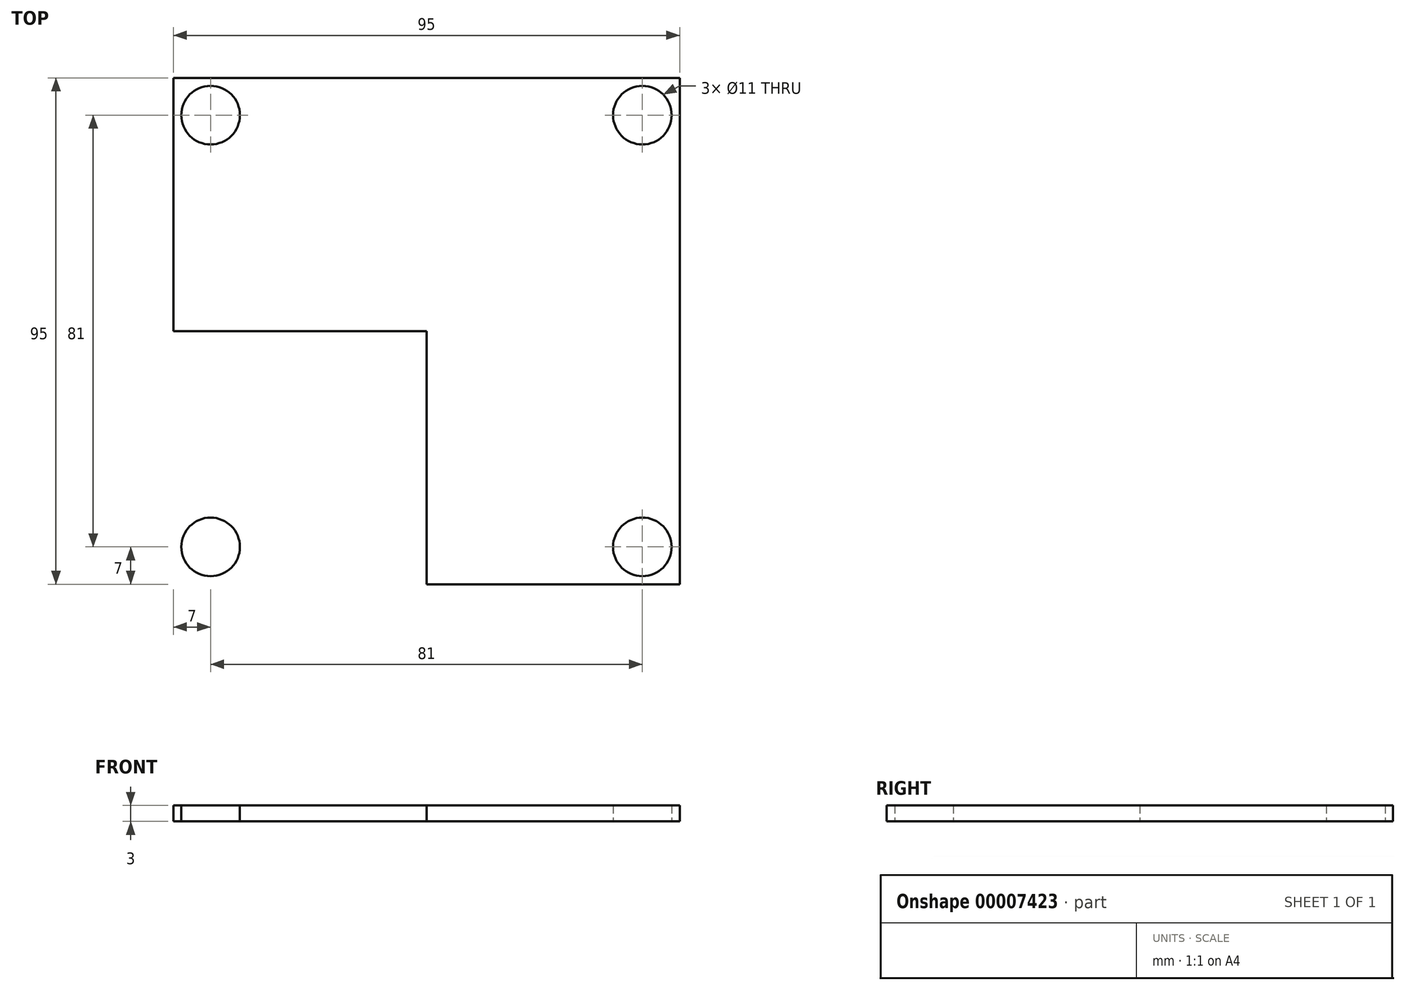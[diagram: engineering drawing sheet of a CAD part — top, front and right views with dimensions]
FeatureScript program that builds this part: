
annotation { "Feature Type Name" : "Feature", "Feature Type Description" : "" }
export const myFeature = defineFeature(function(context is Context, id is Id, definition is map)
    precondition{}
    {
        {
            var Q0;
            Q0=qCreatedBy(makeId("Top.planeOp"),FACE);
            var sketch = newSketch(context, id + "F0", { "sketchPlane" : qUnion([Q0])});
            skLineSegment(sketch, "E0.rect.bottom", {"start": v(47.5, 47.5) * mm, "end": v(-47.5, 47.5) * mm});
            skLineSegment(sketch, "E0.rect.top", {"start": v(47.5, -47.5) * mm, "end": v(-47.5, -47.5) * mm});
            skLineSegment(sketch, "E0.rect.left", {"start": v(47.5, 47.5) * mm, "end": v(47.5, -47.5) * mm});
            skLineSegment(sketch, "E0.rect.right", {"start": v(-47.5, 47.5) * mm, "end": v(-47.5, -47.5) * mm});
            skPoint(sketch, "E0.rect.middle", {"position": v(0, 0) * mm});
            skLineSegment(sketch, "E1", {"start": v(-47.5, 40.5) * mm, "end": v(47.5, 40.5) * mm});
            skLineSegment(sketch, "E2", {"start": v(-40.5, 47.5) * mm, "end": v(-40.5, 40.5) * mm});
            skLineSegment(sketch, "E3", {"start": v(-40.5, 44) * mm, "end": v(-47.5, 44) * mm});
            skCircle(sketch, "E4", {"center": v(-40.5, 40.5) * mm, "radius": 5.5 * mm});
            skLineSegment(sketch, "E5", {"start": v(0, 47.5) * mm, "end": v(0, -47.5) * mm});
            skLineSegment(sketch, "E6", {"start": v(-47.5, 0) * mm, "end": v(47.5, 0) * mm});
            skCircle(sketch, "E7.0.MirrorC", {"center": v(40.5, 40.5) * mm, "radius": 5.5 * mm});
            skCircle(sketch, "E8.0.MirrorC", {"center": v(-40.5, -40.5) * mm, "radius": 5.5 * mm});
            skCircle(sketch, "E9.0.MirrorC", {"center": v(40.5, -40.5) * mm, "radius": 5.5 * mm});
            skSolve(sketch);
        }
        {
            var Q0;
            {var subQ3=sQuery(id+"F0.wireOp",EDGE,"E0.rect.right");var subQ5=sQuery(id+"F0.wireOp",EDGE,"E1");var subQ10=makeQuery(id+"F0.imprint","INTERSECT",VERTEX,{"derivedFrom":[subQ3,subQ5]});Q0=makeQuery(id+"F0.imprint","IMPRINT",FACE,{"disambiguationData":[TD([[makeQuery(id+"F0.imprint","IMPRINT",EDGE,{"disambiguationData":[TD([[subQ10,-1.0]])],"derivedFrom":subQ3}),1.0]])]});}
            var Q1;
            {var subQ3=sQuery(id+"F0.wireOp",EDGE,"E0.rect.left");var subQ5=sQuery(id+"F0.wireOp",EDGE,"E1");var subQ10=makeQuery(id+"F0.imprint","INTERSECT",VERTEX,{"derivedFrom":[subQ3,subQ5]});Q1=makeQuery(id+"F0.imprint","IMPRINT",FACE,{"disambiguationData":[TD([[makeQuery(id+"F0.imprint","IMPRINT",EDGE,{"disambiguationData":[TD([[subQ10,-1.0]])],"derivedFrom":subQ3}),-1.0]])]});}
            var Q2;
            {var subQ6=sQuery(id+"F0.wireOp",EDGE,"E0.rect.bottom");var subQ8=sQuery(id+"F0.wireOp",EDGE,"E0.rect.left");var subQ10=makeQuery(id+"F0.imprint","INTERSECT",VERTEX,{"derivedFrom":[subQ6,subQ8]});Q2=makeQuery(id+"F0.imprint","IMPRINT",FACE,{"disambiguationData":[TD([[makeQuery(id+"F0.imprint","IMPRINT",EDGE,{"disambiguationData":[TD([[subQ10,-1.0]])],"derivedFrom":subQ6}),1.0]])]});}
            var Q3;
            {var subQ3=sQuery(id+"F0.wireOp",EDGE,"E0.rect.bottom");var subQ6=sQuery(id+"F0.wireOp",EDGE,"E2");var subQ9=makeQuery(id+"F0.imprint","INTERSECT",VERTEX,{"derivedFrom":[subQ3,subQ6]});Q3=makeQuery(id+"F0.imprint","IMPRINT",FACE,{"disambiguationData":[TD([[makeQuery(id+"F0.imprint","IMPRINT",EDGE,{"disambiguationData":[TD([[subQ9,1.0]])],"derivedFrom":subQ3}),1.0]])]});}
            var Q4;
            {var subQ5=sQuery(id+"F0.wireOp",EDGE,"E0.rect.right");var subQ7=sQuery(id+"F0.wireOp",EDGE,"E0.rect.bottom");var subQ9=makeQuery(id+"F0.imprint","INTERSECT",VERTEX,{"derivedFrom":[subQ7,subQ5]});Q4=makeQuery(id+"F0.imprint","IMPRINT",FACE,{"disambiguationData":[TD([[makeQuery(id+"F0.imprint","IMPRINT",EDGE,{"disambiguationData":[TD([[subQ9,1.0]])],"derivedFrom":subQ7}),1.0]])]});}
            var Q5;
            {var subQ3=sQuery(id+"F0.wireOp",EDGE,"E1");var subQ5=sQuery(id+"F0.wireOp",EDGE,"E0.rect.right");var subQ7=makeQuery(id+"F0.imprint","INTERSECT",VERTEX,{"derivedFrom":[subQ5,subQ3]});Q5=makeQuery(id+"F0.imprint","IMPRINT",FACE,{"disambiguationData":[TD([[makeQuery(id+"F0.imprint","IMPRINT",EDGE,{"disambiguationData":[TD([[subQ7,1.0]])],"derivedFrom":subQ5}),1.0]])]});}
            var Q6;
            Q6=makeQuery(id+"F0.imprint","IMPRINT",FACE,{"disambiguationData":[TD([[makeQuery(id+"F0.imprint","IMPRINT",EDGE,{"derivedFrom":sQuery(id+"F0.wireOp",EDGE,"E8.0.MirrorC")}),1.0]])]});
            var Q7;
            Q7=makeQuery(id+"F0.imprint","IMPRINT",FACE,{"disambiguationData":[TD([[makeQuery(id+"F0.imprint","IMPRINT",EDGE,{"derivedFrom":sQuery(id+"F0.wireOp",EDGE,"E9.0.MirrorC")}),-1.0]])]});
            extrude(context, id + "F1", {"entities" : qUnion([Q0, Q1, Q2, Q3, Q4, Q5, Q6, Q7]), "depth" : 3 * mm});
        }
        {
            var Q0;
            Q0=makeQuery(id+"F1.opExtrude","CAP_FACE",FACE,{"disambiguationData":[OSD([sQuery(id+"F0.wireOp",EDGE,"E0.rect.bottom"),sQuery(id+"F0.wireOp",EDGE,"E0.rect.top"),sQuery(id+"F0.wireOp",EDGE,"E0.rect.left"),sQuery(id+"F0.wireOp",EDGE,"E0.rect.right"),sQuery(id+"F0.wireOp",EDGE,"E4"),sQuery(id+"F0.wireOp",EDGE,"E7.0.MirrorC"),sQuery(id+"F0.wireOp",EDGE,"E8.0.MirrorC"),sQuery(id+"F0.wireOp",EDGE,"E9.0.MirrorC")])],"isStart":false});
            var sketch = newSketch(context, id + "F2", { "sketchPlane" : qUnion([Q0])});
            skCircle(sketch, "E10", {"center": v(0, 0) * mm, "radius": 47.5 * mm, "construction": true});
            skCircle(sketch, "E11", {"center": v(0, 0) * mm, "radius": 46 * mm, "construction": true});
            skPoint(sketch, "E12", {"position": v(-39.7, -23.24) * mm});
            skCircle(sketch, "E13", {"center": v(-39.7, -23.24) * mm, "radius": 2 * mm});
            skSolve(sketch);
        }
        {
            var Q0;
            Q0=makeQuery(id+"F2.imprint","IMPRINT",FACE,{"disambiguationData":[TD([[makeQuery(id+"F2.imprint","IMPRINT",EDGE,{"derivedFrom":sQuery(id+"F2.wireOp",EDGE,"E13")}),1.0]])]});
            extrude(context, id + "F3", {"entities" : qUnion([Q0]), "operationType" : NewBodyOperationType.REMOVE, "endBound" : BoundingType.THROUGH_ALL, "oppositeDirection" : true, "depth" : 25 * mm});
        }
    });
